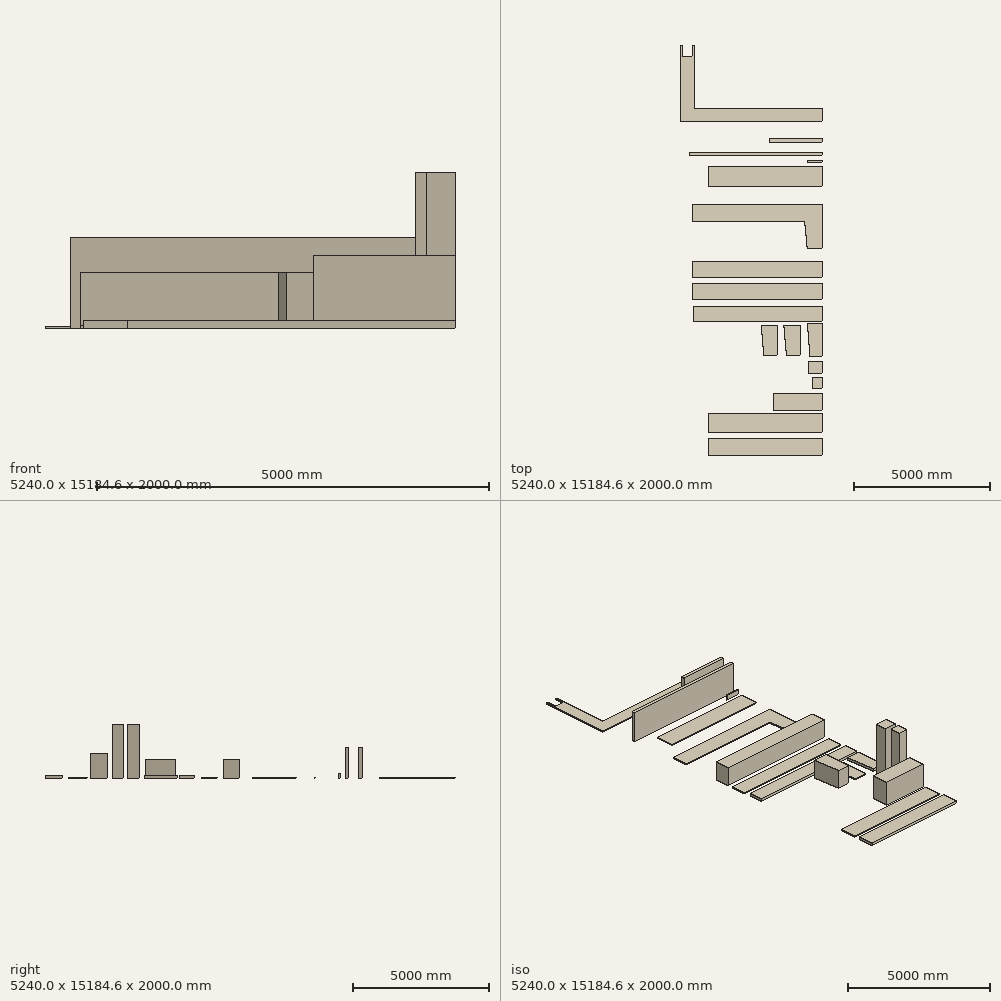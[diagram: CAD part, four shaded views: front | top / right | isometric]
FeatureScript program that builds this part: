
annotation { "Feature Type Name" : "Feature", "Feature Type Description" : "" }
export const myFeature = defineFeature(function(context is Context, id is Id, definition is map)
    precondition{}
    {
        {
            var Q0;
            Q0=qCreatedBy(makeId("Top.planeOp"),FACE);
            var sketch = newSketch(context, id + "F0", { "sketchPlane" : qUnion([Q0])});
            skLineSegment(sketch, "E0.bottom", {"start": v(0, 0) * mm, "end": v(-4195, 0) * mm});
            skLineSegment(sketch, "E0.top", {"start": v(0, -625) * mm, "end": v(-4195, -625) * mm});
            skLineSegment(sketch, "E0.left", {"start": v(0, 0) * mm, "end": v(0, -625) * mm});
            skLineSegment(sketch, "E0.right", {"start": v(-4195, 0) * mm, "end": v(-4195, -625) * mm});
            skSolve(sketch);
        }
        {
            var Q0;
            Q0 = qSketchRegion(id + "F0", true);
            extrude(context, id + "F1", {"entities" : qUnion([Q0]), "depth" : 100 * mm});
        }
        {
            var Q0;
            Q0=qCreatedBy(makeId("Top.planeOp"),FACE);
            var sketch = newSketch(context, id + "F2", { "sketchPlane" : qUnion([Q0])});
            skLineSegment(sketch, "E1.bottom", {"start": v(0, 238) * mm, "end": v(-4195, 238) * mm});
            skLineSegment(sketch, "E1.top", {"start": v(0, 913) * mm, "end": v(-4195, 913) * mm});
            skLineSegment(sketch, "E1.left", {"start": v(0, 238) * mm, "end": v(0, 913) * mm});
            skLineSegment(sketch, "E1.right", {"start": v(-4195, 238) * mm, "end": v(-4195, 913) * mm});
            skSolve(sketch);
        }
        {
            var Q0;
            Q0=makeQuery(id+"F2.imprint","IMPRINT",FACE,{"disambiguationData":[TD([[makeQuery(id+"F2.imprint","IMPRINT",EDGE,{"derivedFrom":sQuery(id+"F2.wireOp",EDGE,"E1.bottom")}),-1.0]])]});
            extrude(context, id + "F3", {"entities" : qUnion([Q0]), "depth" : 40 * mm});
        }
        {
            var Q0;
            Q0=qCreatedBy(makeId("Top.planeOp"),FACE);
            var sketch = newSketch(context, id + "F4", { "sketchPlane" : qUnion([Q0])});
            skLineSegment(sketch, "E2.bottom", {"start": v(0, 1033.95) * mm, "end": v(-1820, 1033.95) * mm});
            skLineSegment(sketch, "E2.top", {"start": v(0, 1683.95) * mm, "end": v(-1820, 1683.95) * mm});
            skLineSegment(sketch, "E2.left", {"start": v(0, 1033.95) * mm, "end": v(0, 1683.95) * mm});
            skLineSegment(sketch, "E2.right", {"start": v(-1820, 1033.95) * mm, "end": v(-1820, 1683.95) * mm});
            skSolve(sketch);
        }
        {
            var Q0;
            Q0 = qSketchRegion(id + "F4", true);
            extrude(context, id + "F5", {"entities" : qUnion([Q0]), "depth" : 930 * mm});
        }
        {
            var Q0;
            Q0=qCreatedBy(makeId("Top.planeOp"),FACE);
            var sketch = newSketch(context, id + "F6", { "sketchPlane" : qUnion([Q0])});
            skLineSegment(sketch, "E3.bottom", {"start": v(0, 1847) * mm, "end": v(-375, 1847) * mm});
            skLineSegment(sketch, "E3.top", {"start": v(0, 2257) * mm, "end": v(-375, 2257) * mm});
            skLineSegment(sketch, "E3.left", {"start": v(0, 1847) * mm, "end": v(0, 2257) * mm});
            skLineSegment(sketch, "E3.right", {"start": v(-375, 1847) * mm, "end": v(-375, 2257) * mm});
            skSolve(sketch);
        }
        {
            var Q0;
            Q0=makeQuery(id+"F6.imprint","IMPRINT",FACE,{"disambiguationData":[TD([[makeQuery(id+"F6.imprint","IMPRINT",EDGE,{"derivedFrom":sQuery(id+"F6.wireOp",EDGE,"E3.bottom")}),-1.0]])]});
            extrude(context, id + "F7", {"entities" : qUnion([Q0]), "depth" : 2000 * mm});
        }
        {
            var Q0;
            Q0=qCreatedBy(makeId("Top.planeOp"),FACE);
            var sketch = newSketch(context, id + "F8", { "sketchPlane" : qUnion([Q0])});
            skLineSegment(sketch, "E4.bottom", {"start": v(0, 2415.82) * mm, "end": v(-505, 2415.82) * mm});
            skLineSegment(sketch, "E4.top", {"start": v(0, 2850.82) * mm, "end": v(-505, 2850.82) * mm});
            skLineSegment(sketch, "E4.left", {"start": v(0, 2415.82) * mm, "end": v(0, 2850.82) * mm});
            skLineSegment(sketch, "E4.right", {"start": v(-505, 2415.82) * mm, "end": v(-505, 2850.82) * mm});
            skSolve(sketch);
        }
        {
            var Q0;
            Q0=makeQuery(id+"F8.imprint","IMPRINT",FACE,{"disambiguationData":[TD([[makeQuery(id+"F8.imprint","IMPRINT",EDGE,{"derivedFrom":sQuery(id+"F8.wireOp",EDGE,"E4.bottom")}),-1.0]])]});
            extrude(context, id + "F9", {"entities" : qUnion([Q0]), "depth" : 2000 * mm});
        }
        {
            var Q0;
            Q0=qCreatedBy(makeId("Top.planeOp"),FACE);
            var sketch = newSketch(context, id + "F10", { "sketchPlane" : qUnion([Q0])});
            skLineSegment(sketch, "E5.bottom", {"start": v(0, 3051.08) * mm, "end": v(-455, 3051.08) * mm});
            skLineSegment(sketch, "E5.top", {"start": v(0, 4251.08) * mm, "end": v(-550, 4251.08) * mm});
            skLineSegment(sketch, "E5.left", {"start": v(0, 3051.08) * mm, "end": v(0, 4251.08) * mm});
            skLineSegment(sketch, "E6", {"start": v(-550, 4251.08) * mm, "end": v(-455, 3051.08) * mm});
            skSolve(sketch);
        }
        {
            var Q0;
            Q0 = qSketchRegion(id + "F10", true);
            extrude(context, id + "F11", {"entities" : qUnion([Q0]), "depth" : 100 * mm});
        }
        {
            var Q0;
            Q0=qCreatedBy(makeId("Top.planeOp"),FACE);
            var sketch = newSketch(context, id + "F12", { "sketchPlane" : qUnion([Q0])});
            skLineSegment(sketch, "E7.bottom", {"start": v(0, 4333.73) * mm, "end": v(-4750, 4333.73) * mm});
            skLineSegment(sketch, "E7.top", {"start": v(0, 4883.73) * mm, "end": v(-4750, 4883.73) * mm});
            skLineSegment(sketch, "E7.left", {"start": v(0, 4333.73) * mm, "end": v(0, 4883.73) * mm});
            skLineSegment(sketch, "E7.right", {"start": v(-4750, 4333.73) * mm, "end": v(-4750, 4883.73) * mm});
            skSolve(sketch);
        }
        {
            var Q0;
            Q0 = qSketchRegion(id + "F12", true);
            extrude(context, id + "F13", {"entities" : qUnion([Q0]), "depth" : 100 * mm});
        }
        {
            var Q0;
            Q0=qCreatedBy(makeId("Top.planeOp"),FACE);
            var sketch = newSketch(context, id + "F14", { "sketchPlane" : qUnion([Q0])});
            skLineSegment(sketch, "E8.bottom", {"start": v(0, 5144.02) * mm, "end": v(-4790, 5144.02) * mm});
            skLineSegment(sketch, "E8.top", {"start": v(0, 5744.02) * mm, "end": v(-4790, 5744.02) * mm});
            skLineSegment(sketch, "E8.left", {"start": v(0, 5144.02) * mm, "end": v(0, 5744.02) * mm});
            skLineSegment(sketch, "E8.right", {"start": v(-4790, 5144.02) * mm, "end": v(-4790, 5744.02) * mm});
            skSolve(sketch);
        }
        {
            var Q0;
            Q0=makeQuery(id+"F14.imprint","IMPRINT",FACE,{"disambiguationData":[TD([[makeQuery(id+"F14.imprint","IMPRINT",EDGE,{"derivedFrom":sQuery(id+"F14.wireOp",EDGE,"E8.bottom")}),-1.0]])]});
            extrude(context, id + "F15", {"entities" : qUnion([Q0]), "depth" : 40 * mm});
        }
        {
            var Q0;
            Q0=qCreatedBy(makeId("Top.planeOp"),FACE);
            var sketch = newSketch(context, id + "F16", { "sketchPlane" : qUnion([Q0])});
            skLineSegment(sketch, "E9.bottom", {"start": v(-821.75, 3081.68) * mm, "end": v(-1326.75, 3081.68) * mm});
            skLineSegment(sketch, "E9.top", {"start": v(-821.75, 4181.68) * mm, "end": v(-1421.75, 4181.68) * mm});
            skLineSegment(sketch, "E9.left", {"start": v(-821.75, 3081.68) * mm, "end": v(-821.75, 4181.68) * mm});
            skLineSegment(sketch, "E10", {"start": v(-1421.75, 4181.68) * mm, "end": v(-1326.75, 3081.68) * mm});
            skSolve(sketch);
        }
        {
            var Q0;
            Q0=makeQuery(id+"F16.imprint","IMPRINT",FACE,{"disambiguationData":[TD([[makeQuery(id+"F16.imprint","IMPRINT",EDGE,{"derivedFrom":sQuery(id+"F16.wireOp",EDGE,"E9.bottom")}),-1.0]])]});
            extrude(context, id + "F17", {"entities" : qUnion([Q0]), "depth" : 40 * mm});
        }
        {
            var Q0;
            Q0=qCreatedBy(makeId("Top.planeOp"),FACE);
            var sketch = newSketch(context, id + "F18", { "sketchPlane" : qUnion([Q0])});
            skLineSegment(sketch, "E11.bottom", {"start": v(-1659.6, 3071.19) * mm, "end": v(-2164.6, 3071.19) * mm});
            skLineSegment(sketch, "E11.top", {"start": v(-1659.6, 4171.19) * mm, "end": v(-2259.6, 4171.19) * mm});
            skLineSegment(sketch, "E11.left", {"start": v(-1659.6, 3071.19) * mm, "end": v(-1659.6, 4171.19) * mm});
            skLineSegment(sketch, "E12", {"start": v(-2259.6, 4171.19) * mm, "end": v(-2164.6, 3071.19) * mm});
            skSolve(sketch);
        }
        {
            var Q0;
            Q0 = qSketchRegion(id + "F18", true);
            extrude(context, id + "F19", {"entities" : qUnion([Q0]), "depth" : 720 * mm});
        }
        {
            var Q0;
            Q0=qCreatedBy(makeId("Top.planeOp"),FACE);
            var sketch = newSketch(context, id + "F20", { "sketchPlane" : qUnion([Q0])});
            skLineSegment(sketch, "E13.bottom", {"start": v(0, 5954.48) * mm, "end": v(-4790, 5954.48) * mm});
            skLineSegment(sketch, "E13.top", {"start": v(0, 6554.48) * mm, "end": v(-4790, 6554.48) * mm});
            skLineSegment(sketch, "E13.left", {"start": v(0, 5954.48) * mm, "end": v(0, 6554.48) * mm});
            skLineSegment(sketch, "E13.right", {"start": v(-4790, 5954.48) * mm, "end": v(-4790, 6554.48) * mm});
            skSolve(sketch);
        }
        {
            var Q0;
            Q0 = qSketchRegion(id + "F20", true);
            extrude(context, id + "F21", {"entities" : qUnion([Q0]), "depth" : 720 * mm});
        }
        {
            var Q0;
            Q0=qCreatedBy(makeId("Top.planeOp"),FACE);
            var sketch = newSketch(context, id + "F22", { "sketchPlane" : qUnion([Q0])});
            skLineSegment(sketch, "E14", {"start": v(0, 7027.3) * mm, "end": v(-555, 7027.3) * mm});
            skLineSegment(sketch, "E15", {"start": v(-650, 8027.3) * mm, "end": v(-4790, 8027.3) * mm});
            skLineSegment(sketch, "E16", {"start": v(-4790, 8027.3) * mm, "end": v(-4790, 8677.3) * mm});
            skLineSegment(sketch, "E17", {"start": v(-4790, 8677.3) * mm, "end": v(0, 8677.3) * mm});
            skLineSegment(sketch, "E18", {"start": v(0, 8677.3) * mm, "end": v(0, 7027.3) * mm});
            skLineSegment(sketch, "E19", {"start": v(-650, 8027.3) * mm, "end": v(-555, 7027.3) * mm});
            skSolve(sketch);
        }
        {
            var Q0;
            Q0 = qSketchRegion(id + "F22", true);
            extrude(context, id + "F23", {"entities" : qUnion([Q0]), "depth" : 40 * mm});
        }
        {
            var Q0;
            Q0=qCreatedBy(makeId("Top.planeOp"),FACE);
            var sketch = newSketch(context, id + "F24", { "sketchPlane" : qUnion([Q0])});
            skLineSegment(sketch, "E20.bottom", {"start": v(0, 9337.91) * mm, "end": v(-4195, 9337.91) * mm});
            skLineSegment(sketch, "E20.top", {"start": v(0, 10062.91) * mm, "end": v(-4195, 10062.91) * mm});
            skLineSegment(sketch, "E20.left", {"start": v(0, 9337.91) * mm, "end": v(0, 10062.91) * mm});
            skLineSegment(sketch, "E20.right", {"start": v(-4195, 9337.91) * mm, "end": v(-4195, 10062.91) * mm});
            skSolve(sketch);
        }
        {
            var Q0;
            Q0 = qSketchRegion(id + "F24", true);
            extrude(context, id + "F25", {"entities" : qUnion([Q0]), "depth" : 40 * mm});
        }
        {
            var Q0;
            Q0=qCreatedBy(makeId("Top.planeOp"),FACE);
            var sketch = newSketch(context, id + "F26", { "sketchPlane" : qUnion([Q0])});
            skLineSegment(sketch, "E21.bottom", {"start": v(0, 10287.28) * mm, "end": v(-555, 10287.28) * mm});
            skLineSegment(sketch, "E21.top", {"start": v(0, 10237.28) * mm, "end": v(-555, 10237.28) * mm});
            skLineSegment(sketch, "E21.left", {"start": v(0, 10237.28) * mm, "end": v(0, 10287.28) * mm});
            skLineSegment(sketch, "E21.right", {"start": v(-555, 10237.28) * mm, "end": v(-555, 10287.28) * mm});
            skSolve(sketch);
        }
        {
            var Q0;
            Q0 = qSketchRegion(id + "F26", true);
            extrude(context, id + "F27", {"entities" : qUnion([Q0]), "depth" : 190 * mm});
        }
        {
            var Q0;
            Q0=makeQuery(id+"F25.opExtrude","SWEPT_FACE",FACE,{"disambiguationData":[OSD([sQuery(id+"F24.wireOp",EDGE,"E20.left")])]});
            var sketch = newSketch(context, id + "F28", { "sketchPlane" : qUnion([Q0])});
            skLineSegment(sketch, "E22.bottom", {"start": v(10062.91, 0) * mm, "end": v(9362.91, 0) * mm});
            skLineSegment(sketch, "E22.top", {"start": v(10062.91, 20) * mm, "end": v(9362.91, 20) * mm});
            skLineSegment(sketch, "E22.left", {"start": v(10062.91, 0) * mm, "end": v(10062.91, 20) * mm});
            skLineSegment(sketch, "E22.right", {"start": v(9362.91, 0) * mm, "end": v(9362.91, 20) * mm});
            skSolve(sketch);
        }
        {
            var Q0;
            Q0 = qSketchRegion(id + "F28", true);
            extrude(context, id + "F29", {"entities" : qUnion([Q0]), "operationType" : NewBodyOperationType.REMOVE, "endBound" : BoundingType.THROUGH_ALL, "oppositeDirection" : true, "depth" : 25 * mm});
        }
        {
            var Q0;
            Q0=makeQuery(id+"F25.opExtrude","CAP_EDGE",EDGE,{"disambiguationData":[OSD([sQuery(id+"F24.wireOp",EDGE,"E20.bottom")])],"isStart":false});
            fillet(context, id + "F30", {"entities" : qUnion([Q0]), "radius" : 10 * mm, "tangentPropagation" : true, "allowEdgeOverflow" : false});
        }
        {
            var Q0;
            Q0=qCreatedBy(makeId("Top.planeOp"),FACE);
            var sketch = newSketch(context, id + "F31", { "sketchPlane" : qUnion([Q0])});
            skLineSegment(sketch, "E23.bottom", {"start": v(0, 10478.42) * mm, "end": v(-4925, 10478.42) * mm});
            skLineSegment(sketch, "E23.top", {"start": v(0, 10613.42) * mm, "end": v(-4925, 10613.42) * mm});
            skLineSegment(sketch, "E23.left", {"start": v(0, 10478.42) * mm, "end": v(0, 10613.42) * mm});
            skLineSegment(sketch, "E23.right", {"start": v(-4925, 10478.42) * mm, "end": v(-4925, 10613.42) * mm});
            skSolve(sketch);
        }
        {
            var Q0;
            Q0 = qSketchRegion(id + "F31", true);
            extrude(context, id + "F32", {"entities" : qUnion([Q0]), "depth" : 1165 * mm});
        }
        {
            var Q0;
            Q0=qCreatedBy(makeId("Top.planeOp"),FACE);
            var sketch = newSketch(context, id + "F33", { "sketchPlane" : qUnion([Q0])});
            skLineSegment(sketch, "E24.bottom", {"start": v(0, 10978.38) * mm, "end": v(-1965, 10978.38) * mm});
            skLineSegment(sketch, "E24.top", {"start": v(0, 11113.38) * mm, "end": v(-1965, 11113.38) * mm});
            skLineSegment(sketch, "E24.left", {"start": v(0, 10978.38) * mm, "end": v(0, 11113.38) * mm});
            skLineSegment(sketch, "E24.right", {"start": v(-1965, 10978.38) * mm, "end": v(-1965, 11113.38) * mm});
            skSolve(sketch);
        }
        {
            var Q0;
            Q0 = qSketchRegion(id + "F33", true);
            extrude(context, id + "F34", {"entities" : qUnion([Q0]), "depth" : 1165 * mm});
        }
        {
            var Q0;
            Q0=qCreatedBy(makeId("Top.planeOp"),FACE);
            var sketch = newSketch(context, id + "F35", { "sketchPlane" : qUnion([Q0])});
            skLineSegment(sketch, "E25", {"start": v(0, 11734.63) * mm, "end": v(-5240, 11734.63) * mm});
            skLineSegment(sketch, "E26", {"start": v(-5240, 11734.63) * mm, "end": v(-5240, 14149.63) * mm});
            skLineSegment(sketch, "E27", {"start": v(-4740, 14559.63) * mm, "end": v(-4740, 12234.63) * mm});
            skLineSegment(sketch, "E28", {"start": v(-4740, 12234.63) * mm, "end": v(0, 12234.63) * mm});
            skLineSegment(sketch, "E29", {"start": v(0, 12234.63) * mm, "end": v(0, 11734.63) * mm});
            skLineSegment(sketch, "E30", {"start": v(-4740, 14559.63) * mm, "end": v(-4791, 14559.63) * mm});
            skLineSegment(sketch, "E31", {"start": v(-4791, 14559.63) * mm, "end": v(-4791, 14149.63) * mm});
            skLineSegment(sketch, "E32", {"start": v(-4791, 14149.63) * mm, "end": v(-5166, 14149.63) * mm});
            skLineSegment(sketch, "E33", {"start": v(-5166, 14149.63) * mm, "end": v(-5166, 14559.63) * mm});
            skLineSegment(sketch, "E34", {"start": v(-5166, 14559.63) * mm, "end": v(-5240, 14559.63) * mm});
            skLineSegment(sketch, "E35", {"start": v(-5240, 14559.63) * mm, "end": v(-5240, 14149.63) * mm});
            skSolve(sketch);
        }
        {
            var Q0;
            Q0 = qSketchRegion(id + "F35", true);
            extrude(context, id + "F36", {"entities" : qUnion([Q0]), "depth" : 35 * mm});
        }
    });
